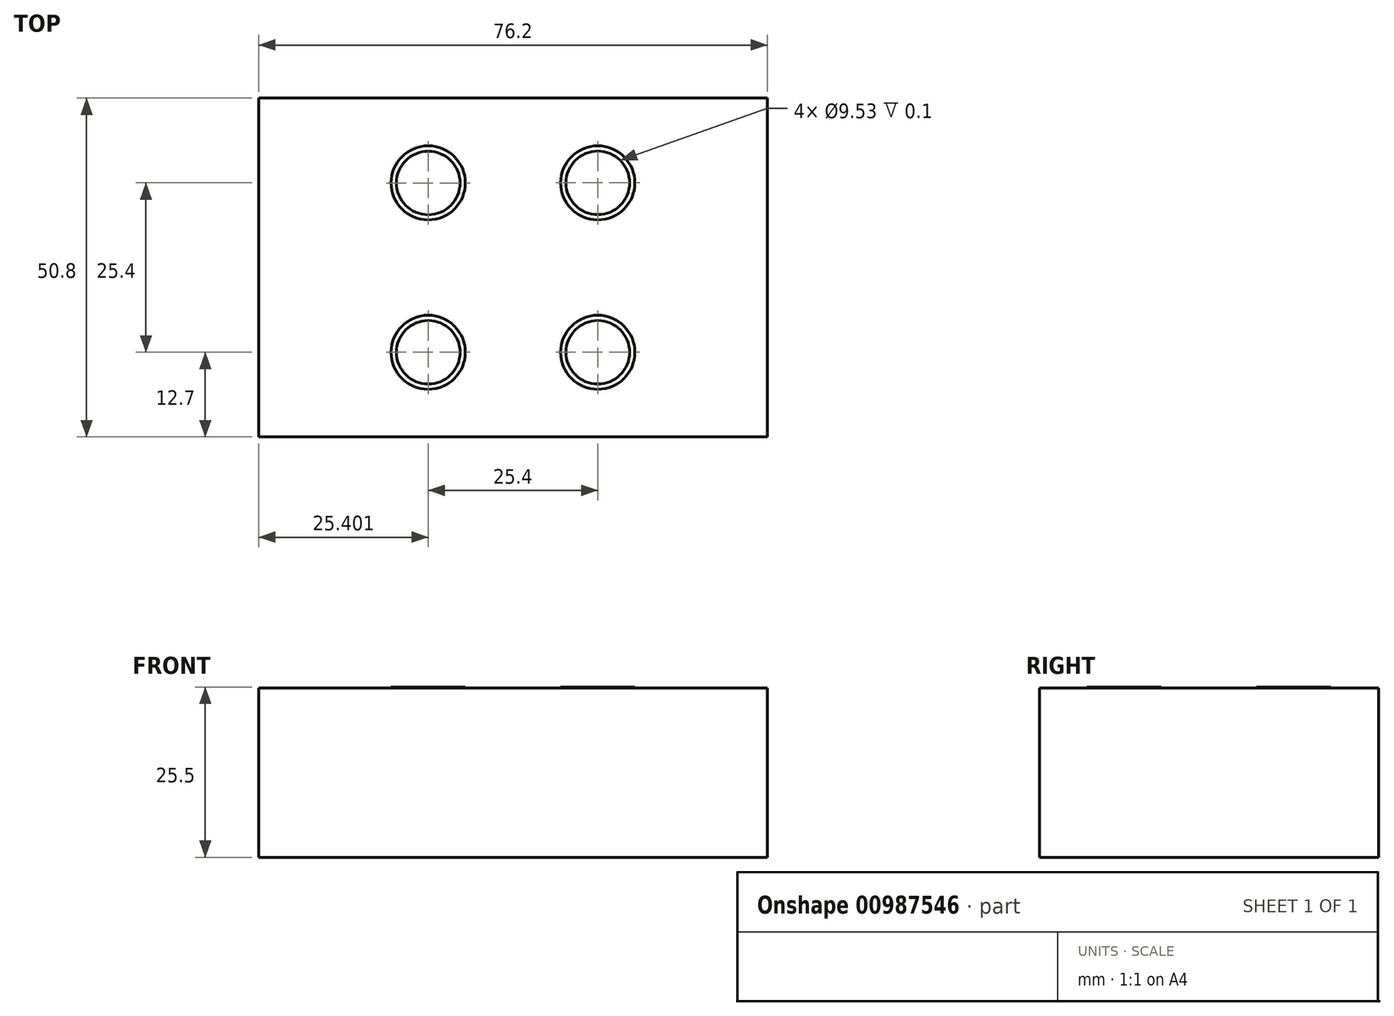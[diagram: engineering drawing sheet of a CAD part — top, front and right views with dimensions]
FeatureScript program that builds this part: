
annotation { "Feature Type Name" : "Feature", "Feature Type Description" : "" }
export const myFeature = defineFeature(function(context is Context, id is Id, definition is map)
    precondition{}
    {
        {
            var Q0;
            Q0=qCreatedBy(makeId("Top.planeOp"),FACE);
            var sketch = newSketch(context, id + "F0", { "sketchPlane" : qUnion([Q0])});
            skLineSegment(sketch, "E0.bottom", {"start": v(-133.08, 50.8) * mm, "end": v(-56.88, 50.8) * mm});
            skLineSegment(sketch, "E0.top", {"start": v(-133.08, 0) * mm, "end": v(-56.88, 0) * mm});
            skLineSegment(sketch, "E0.left", {"start": v(-133.08, 50.8) * mm, "end": v(-133.08, 0) * mm});
            skLineSegment(sketch, "E0.right", {"start": v(-56.88, 50.8) * mm, "end": v(-56.88, 0) * mm});
            skSolve(sketch);
        }
        {
            var Q0;
            Q0 = qSketchRegion(id + "F0", true);
            extrude(context, id + "F1", {"entities" : qUnion([Q0]), "oppositeDirection" : true, "depth" : 25.4 * mm, "offsetDistance" : 25.4 * mm});
        }
        {
            var Q0;
            Q0=makeQuery(id+"F1.opExtrude","CAP_FACE",FACE,{"disambiguationData":[OSD([sQuery(id+"F0.wireOp",EDGE,"E0.bottom"),sQuery(id+"F0.wireOp",EDGE,"E0.top"),sQuery(id+"F0.wireOp",EDGE,"E0.left"),sQuery(id+"F0.wireOp",EDGE,"E0.right")])],"isStart":true});
            var sketch = newSketch(context, id + "F2", { "sketchPlane" : qUnion([Q0])});
            skCircle(sketch, "E1", {"center": v(-107.68, 38.1) * mm, "radius": 5.56 * mm});
            skCircle(sketch, "E2", {"center": v(-82.28, 38.1) * mm, "radius": 5.56 * mm});
            skCircle(sketch, "E3", {"center": v(-107.68, 12.7) * mm, "radius": 5.56 * mm});
            skCircle(sketch, "E4", {"center": v(-82.28, 12.7) * mm, "radius": 5.56 * mm});
            skSolve(sketch);
        }
        {
            var Q0;
            Q0 = qSketchRegion(id + "F2", true);
            extrude(context, id + "F3", {"entities" : qUnion([Q0]), "operationType" : NewBodyOperationType.ADD, "depth" : 0.1 * mm, "offsetDistance" : 25.4 * mm});
        }
        {
            var Q0;
            Q0=makeQuery(id+"F3.opExtrude","CAP_FACE",FACE,{"disambiguationData":[OSD([sQuery(id+"F2.wireOp",EDGE,"E2")])],"isStart":false});
            var sketch = newSketch(context, id + "F4", { "sketchPlane" : qUnion([Q0])});
            skCircle(sketch, "E5", {"center": v(-107.68, 38.1) * mm, "radius": 4.76 * mm});
            skCircle(sketch, "E6", {"center": v(-82.28, 38.1) * mm, "radius": 4.76 * mm});
            skCircle(sketch, "E7", {"center": v(-107.68, 12.7) * mm, "radius": 4.76 * mm});
            skCircle(sketch, "E8", {"center": v(-82.28, 12.7) * mm, "radius": 4.76 * mm});
            skSolve(sketch);
        }
        {
            var Q0;
            Q0 = qSketchRegion(id + "F4", true);
            extrude(context, id + "F5", {"entities" : qUnion([Q0]), "operationType" : NewBodyOperationType.REMOVE, "oppositeDirection" : true, "depth" : 0.1 * mm, "offsetDistance" : 25.4 * mm});
        }
    });
